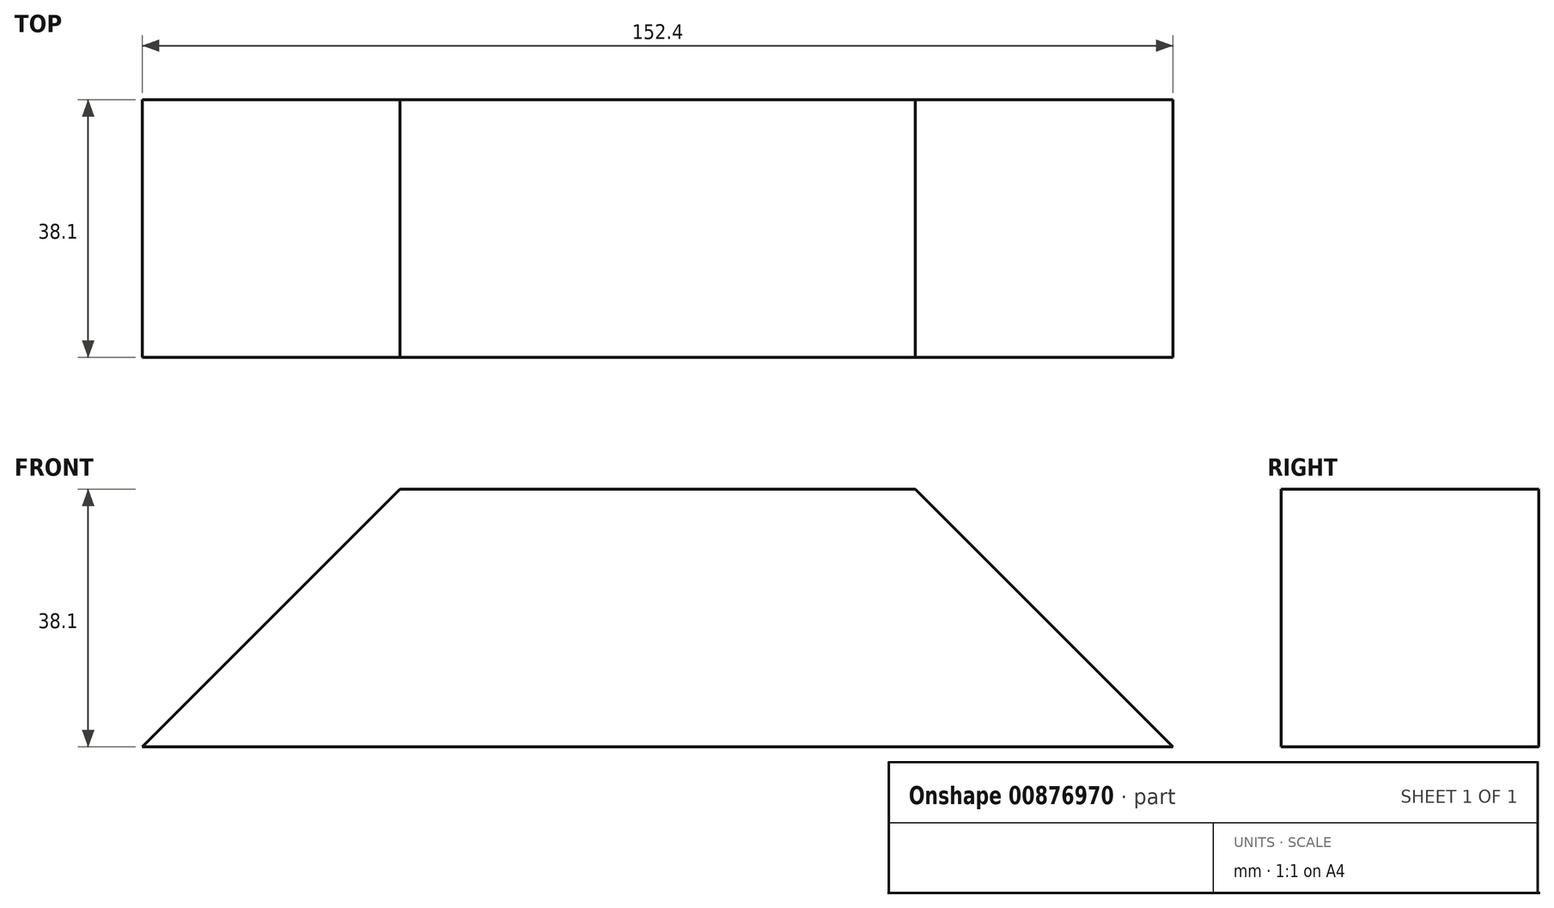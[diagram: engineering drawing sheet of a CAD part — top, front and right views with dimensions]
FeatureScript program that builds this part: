
annotation { "Feature Type Name" : "Feature", "Feature Type Description" : "" }
export const myFeature = defineFeature(function(context is Context, id is Id, definition is map)
    precondition{}
    {
        {
            var Q0;
            Q0=qCreatedBy(makeId("Right.planeOp"),FACE);
            var sketch = newSketch(context, id + "F0", { "sketchPlane" : qUnion([Q0])});
            skLineSegment(sketch, "E0.bottom", {"start": v(19.05, 19.05) * mm, "end": v(-19.05, 19.05) * mm});
            skLineSegment(sketch, "E0.top", {"start": v(19.05, -19.05) * mm, "end": v(-19.05, -19.05) * mm});
            skLineSegment(sketch, "E0.left", {"start": v(19.05, 19.05) * mm, "end": v(19.05, -19.05) * mm});
            skLineSegment(sketch, "E0.right", {"start": v(-19.05, 19.05) * mm, "end": v(-19.05, -19.05) * mm});
            skPoint(sketch, "E0.middle", {"position": v(0, 0) * mm});
            skSolve(sketch);
        }
        {
            var Q0;
            Q0=makeQuery(id+"F0.imprint","IMPRINT",FACE,{"disambiguationData":[TD([[makeQuery(id+"F0.imprint","IMPRINT",EDGE,{"derivedFrom":sQuery(id+"F0.wireOp",EDGE,"E0.bottom")}),1.0]])]});
            extrude(context, id + "F1", {"entities" : qUnion([Q0]), "depth" : 152.4 * mm, "offsetDistance" : 25.4 * mm});
        }
        {
            var Q0;
            Q0=makeQuery(id+"F1.opExtrude","SWEPT_FACE",FACE,{"disambiguationData":[OSD([sQuery(id+"F0.wireOp",EDGE,"E0.right")])]});
            var sketch = newSketch(context, id + "F2", { "sketchPlane" : qUnion([Q0])});
            skLineSegment(sketch, "E1", {"start": v(0, -19.05) * mm, "end": v(38.1, 19.05) * mm});
            skLineSegment(sketch, "E2", {"start": v(38.1, 19.05) * mm, "end": v(0, 19.05) * mm});
            skLineSegment(sketch, "E3", {"start": v(0, 19.05) * mm, "end": v(0, -19.05) * mm});
            skLineSegment(sketch, "E4", {"start": v(152.4, -19.05) * mm, "end": v(114.3, 19.05) * mm});
            skLineSegment(sketch, "E5", {"start": v(114.3, 19.05) * mm, "end": v(152.4, 19.05) * mm});
            skLineSegment(sketch, "E6", {"start": v(152.4, 19.05) * mm, "end": v(152.4, -19.05) * mm});
            skSolve(sketch);
        }
        {
            var Q0;
            Q0=makeQuery(id+"F2.imprint","IMPRINT",FACE,{"disambiguationData":[TD([[makeQuery(id+"F2.imprint","IMPRINT",EDGE,{"derivedFrom":sQuery(id+"F2.wireOp",EDGE,"E1")}),1.0]])]});
            var Q1;
            Q1=makeQuery(id+"F2.imprint","IMPRINT",FACE,{"disambiguationData":[TD([[makeQuery(id+"F2.imprint","IMPRINT",EDGE,{"derivedFrom":sQuery(id+"F2.wireOp",EDGE,"E4")}),-1.0]])]});
            extrude(context, id + "F3", {"entities" : qUnion([Q0, Q1]), "operationType" : NewBodyOperationType.REMOVE, "endBound" : BoundingType.THROUGH_ALL, "oppositeDirection" : true, "depth" : 25.4 * mm, "offsetDistance" : 25.4 * mm});
        }
    });
